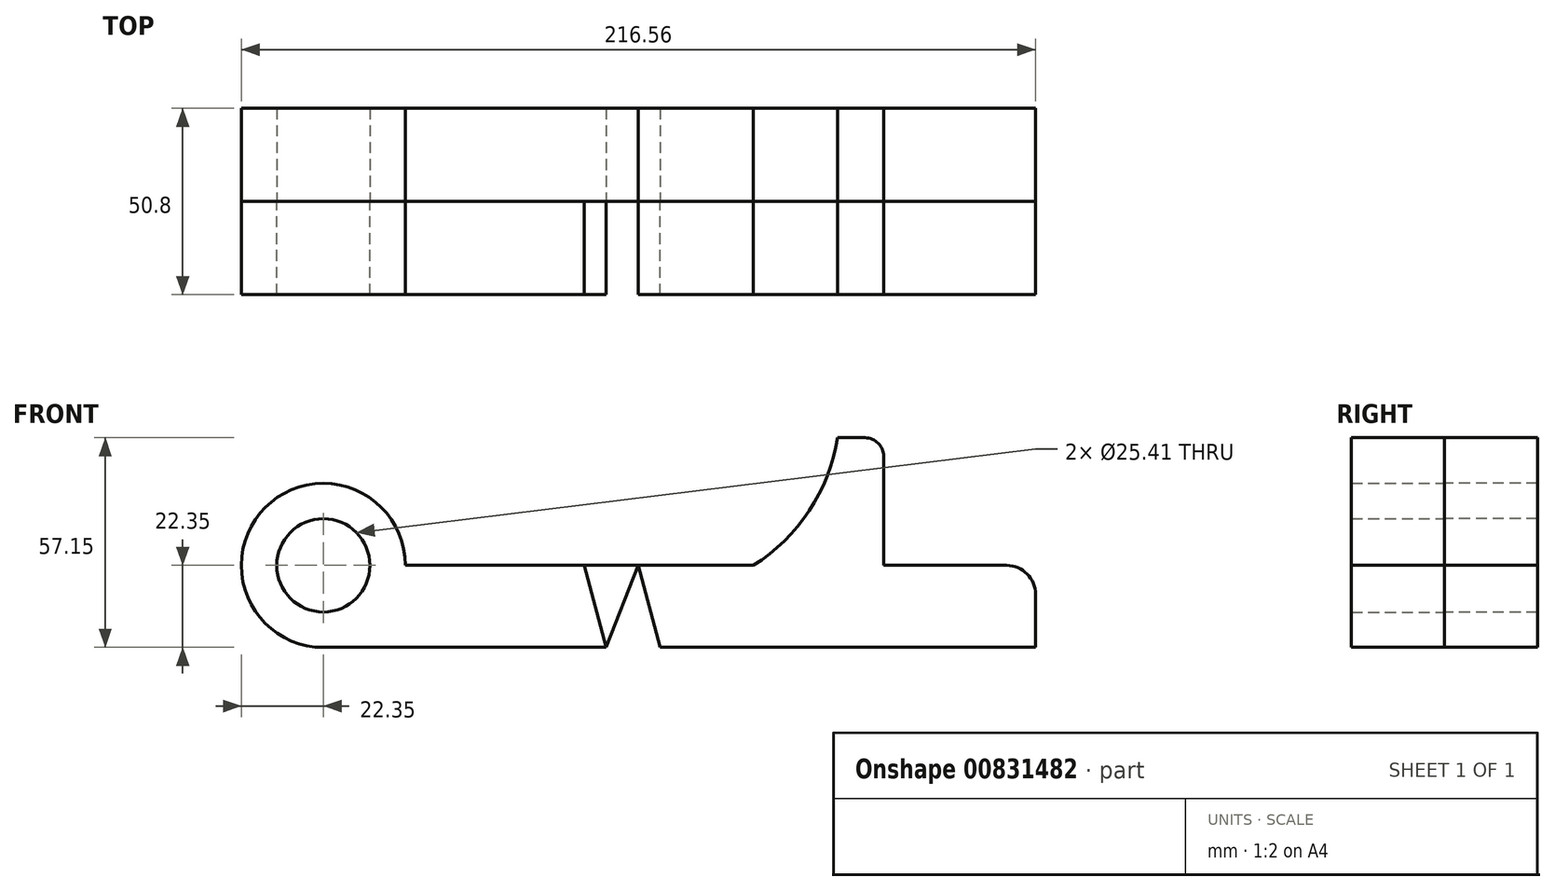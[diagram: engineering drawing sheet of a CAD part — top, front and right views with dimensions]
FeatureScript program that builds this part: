
annotation { "Feature Type Name" : "Feature", "Feature Type Description" : "" }
export const myFeature = defineFeature(function(context is Context, id is Id, definition is map)
    precondition{}
    {
        {
            var Q0;
            Q0=qCreatedBy(makeId("Front.planeOp"),FACE);
            var sketch = newSketch(context, id + "F0", { "sketchPlane" : qUnion([Q0])});
            skCircle(sketch, "E0", {"center": v(0, 0) * mm, "radius": 12.7 * mm});
            skArc(sketch, "E1", {"start": v(22.35, 0) * mm, "mid": v(-15.8, 15.8) * mm, "end": v(0, -22.35) * mm});
            skLineSegment(sketch, "E2", {"start": v(0, -22.35) * mm, "end": v(194.2, -22.35) * mm});
            skLineSegment(sketch, "E3", {"start": v(0, 0) * mm, "end": v(186.33, 0) * mm});
            skLineSegment(sketch, "E4", {"start": v(194.2, -7.87) * mm, "end": v(194.2, -22.35) * mm});
            skLineSegment(sketch, "E5", {"start": v(26.12, 0) * mm, "end": v(40.04, -22.35) * mm});
            skLineSegment(sketch, "E6", {"start": v(71.12, 0) * mm, "end": v(77.09, -22.35) * mm});
            skLineSegment(sketch, "E7", {"start": v(77.09, -22.35) * mm, "end": v(91.85, -22.35) * mm});
            skLineSegment(sketch, "E8", {"start": v(91.85, -22.35) * mm, "end": v(85.88, 0) * mm});
            skLineSegment(sketch, "E9", {"start": v(85.88, 0) * mm, "end": v(77.09, -22.35) * mm});
            skLineSegment(sketch, "E10", {"start": v(117.25, -22.35) * mm, "end": v(117.25, 0) * mm});
            skLineSegment(sketch, "E11", {"start": v(140.25, 34.8) * mm, "end": v(147.71, 34.8) * mm});
            skLineSegment(sketch, "E12", {"start": v(152.8, 29.72) * mm, "end": v(152.8, 0) * mm});
            skArc(sketch, "E13", {"start": v(117.25, 0) * mm, "mid": v(132.49, 14.93) * mm, "end": v(140.25, 34.8) * mm});
            skArc(sketch, "E14.filletArc", {"start": v(152.8, 29.72) * mm, "mid": v(151.3, 33.31) * mm, "end": v(147.71, 34.8) * mm});
            skArc(sketch, "E15.filletArc", {"start": v(194.2, -7.87) * mm, "mid": v(191.9, -2.3) * mm, "end": v(186.33, 0) * mm});
            skSolve(sketch);
        }
        {
            var Q0;
            Q0=makeQuery(id+"F0.imprint","IMPRINT",FACE,{"disambiguationData":[TD([[makeQuery(id+"F0.imprint","IMPRINT",EDGE,{"derivedFrom":sQuery(id+"F0.wireOp",EDGE,"E0")}),-1.0]])]});
            var Q1;
            {var subQ0=sQuery(id+"F0.wireOp",EDGE,"E5");Q1=makeQuery(id+"F0.imprint","IMPRINT",FACE,{"disambiguationData":[TD([[makeQuery(id+"F0.imprint","IMPRINT",EDGE,{"derivedFrom":subQ0}),1.0]])]});}
            var Q2;
            {var subQ0=sQuery(id+"F0.wireOp",EDGE,"E4");Q2=makeQuery(id+"F0.imprint","IMPRINT",FACE,{"disambiguationData":[TD([[makeQuery(id+"F0.imprint","IMPRINT",EDGE,{"derivedFrom":subQ0}),-1.0]])]});}
            var Q3;
            Q3=makeQuery(id+"F0.imprint","IMPRINT",FACE,{"disambiguationData":[TD([[makeQuery(id+"F0.imprint","IMPRINT",EDGE,{"derivedFrom":sQuery(id+"F0.wireOp",EDGE,"E11")}),-1.0]])]});
            var Q4;
            {var subQ0=sQuery(id+"F0.wireOp",EDGE,"E8");Q4=makeQuery(id+"F0.imprint","IMPRINT",FACE,{"disambiguationData":[TD([[makeQuery(id+"F0.imprint","IMPRINT",EDGE,{"derivedFrom":subQ0}),-1.0]])]});}
            extrude(context, id + "F1", {"entities" : qUnion([Q0, Q1, Q2, Q3, Q4]), "depth" : 25.4 * mm, "offsetDistance" : 25.4 * mm});
        }
        {
            var Q0;
            {var subQ0=sQuery(id+"F0.wireOp",EDGE,"E5");Q0=makeQuery(id+"F0.imprint","IMPRINT",FACE,{"disambiguationData":[TD([[makeQuery(id+"F0.imprint","IMPRINT",EDGE,{"derivedFrom":subQ0}),1.0]])]});}
            var Q1;
            Q1=makeQuery(id+"F0.imprint","IMPRINT",FACE,{"disambiguationData":[TD([[makeQuery(id+"F0.imprint","IMPRINT",EDGE,{"derivedFrom":sQuery(id+"F0.wireOp",EDGE,"E0")}),-1.0]])]});
            var Q2;
            {var subQ0=sQuery(id+"F0.wireOp",EDGE,"E8");Q2=makeQuery(id+"F0.imprint","IMPRINT",FACE,{"disambiguationData":[TD([[makeQuery(id+"F0.imprint","IMPRINT",EDGE,{"derivedFrom":subQ0}),-1.0]])]});}
            var Q3;
            {var subQ0=sQuery(id+"F0.wireOp",EDGE,"E4");Q3=makeQuery(id+"F0.imprint","IMPRINT",FACE,{"disambiguationData":[TD([[makeQuery(id+"F0.imprint","IMPRINT",EDGE,{"derivedFrom":subQ0}),-1.0]])]});}
            var Q4;
            Q4=makeQuery(id+"F0.imprint","IMPRINT",FACE,{"disambiguationData":[TD([[makeQuery(id+"F0.imprint","IMPRINT",EDGE,{"derivedFrom":sQuery(id+"F0.wireOp",EDGE,"E11")}),-1.0]])]});
            var Q5;
            {var subQ0=sQuery(id+"F0.wireOp",EDGE,"E6");Q5=makeQuery(id+"F0.imprint","IMPRINT",FACE,{"disambiguationData":[TD([[makeQuery(id+"F0.imprint","IMPRINT",EDGE,{"derivedFrom":subQ0}),1.0]])]});}
            var Q6;
            Q6=makeQuery(id+"F0.imprint","IMPRINT",FACE,{"disambiguationData":[TD([[makeQuery(id+"F0.imprint","IMPRINT",EDGE,{"derivedFrom":sQuery(id+"F0.wireOp",EDGE,"E7")}),1.0]])]});
            extrude(context, id + "F2", {"entities" : qUnion([Q0, Q1, Q2, Q3, Q4, Q5, Q6]), "oppositeDirection" : true, "depth" : 25.4 * mm, "offsetDistance" : 25.4 * mm});
        }
    });
